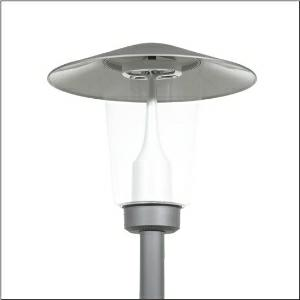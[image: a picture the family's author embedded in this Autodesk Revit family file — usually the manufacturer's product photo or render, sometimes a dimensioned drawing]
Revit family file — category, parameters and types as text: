
# Revit family: pilzleuchte_iq___st1_2a_5xa5235mf14hp_ceaa
name_source: partatom
category: Lighting Fixtures
units: mm (PartAtom-declared; Revit-internal decimal feet)

## family parameters
Cut with Voids When Loaded = No
Host = Face
Light Source = No
Part Type = Normal
Room Calculation Point = No
Round Connector Dimension = Use Diameter
Shared = No

## types (1)
- --- (1 x LED, 4280 lm, 33.6 W, 2700K)
    Apparent Load = 34 VA
    CIE Flux Codes = 23 60 92 98 100
    Color Rendering = 70
    Color Temperature = 2700K
    Default Elevation = 1800 mm
    Description = Mushroom Luminaire iQ, mast luminaire, Module 540 iQ-SR, primary light control with 3 zone facetted reflector, of plastic, silver coated, highly specular, structured, primary optical cover: cover, of PMMA, transparent, light distribution: ST1.2a, light emission: direct distribution, primary light characteristic: asymmetric, installation type: post-top, LED, High Power LED, rated luminous flux: 4.280lm, luminous efficacy: 127lm/W, light colour: 727, colour temperature: 2700K, control gear: iQ Street-Remote, control: pre-setting: logarithmic dimming characteristic, Street-Remote, Auto-Match, Temp-Guard, Lumen-Switch, Night-Set, Smart-Wire, Light-Fading, Desk-Remote (wireless, voltage-free reading and setting of iQ features in the workshop via application-optimized NFC function/RFID function), optimised constant luminous flux control (CLO 2.0), with terminal, 6-pole, max. 2.5mm², mains connection: 230..240V, AC, 50/60Hz, start of lifetime: 34W, end of service life: 36W, reduction: 15W, luminaire housing, upper part, of glass-fibre reinforced polyester, coated, Siteco® metallic grey (DB 702S), diameter: 650mm, height: 586mm, spigot size: d x l = 76 x 70mm (post-top) | with reducer (optional accessory) 60 x 70mm, mounting height: 3..5m, post-top mast mounting element, of diecast aluminium, coated, Siteco® metallic grey (DB 702S), Module 540 iQ-SR, traffic white (RAL 9016), equipment: Power, protection rating (complete): IP65, insulation class (complete): insulation class II (safety insulation), certification: CE, ENEC, VDE, packaging unit: 1 piece

Light Distribution: ST1.2a
    Height = 586 mm
    Lamp = 1 x LED
    Lamp Light Flux = 4280 lm
    Lamp Power = 33.6 W
    Lamp count = 1
    Length = 650 mm
    Luminous efficacy = 127 lm/W
    Manufacturer = Siteco
    ModVariant = No
    Model = 5XA5235MF14HP
    Number of Poles = 1
    OnlyDefault = Yes
    Power Factor = 1
    Product Name = Pilzleuchte iQ | ST1.2a
    Product group = mast luminaire | pylon top
    ProductGroupID = 6100
    Protection Class = Protection class II
    Protection Degree = IP 65
    RLX_Detail_Level = 1
    RLX_Emergency_Light_Flux = 0 lm
    RLX_Emergency_Type = 0
    RLX_Emergency_Type_DB = No
    RlxData = <blob elided: 51469 chars, md5=4490bda5>
    Socket = socket
    Standby Power = 0 W
    System Light Flux = 4280 lm
    System Power = 34 W
    Type Comments = factory setting: luminous flux: 100 % | dim-lin: 254 | 695 mA
    Type Image = l_1006077.jpg
    URL = http://relux.com
    VarID = @adj_152261
    Voltage = 0 V
    Weight = 0.00 kg
    Width = 0 mm  [stored 0 ft]

note: [stored X ft] marks values corroborated as IEEE doubles in the binary element streams (Revit-internal decimal feet)

## geometry (parser evidence)
native form markers: Blend x4, Sweep x9
no freeform markers — native parametric forms only
